# Revit family: Train_Rack-American_Standard-Town_Square-7455260_Series
name_source: partatom
category: Specialty Equipment
units: mm (PartAtom-declared; Revit-internal decimal feet)

## family parameters
Cut with Voids When Loaded = No
Host = Face
OmniClass Number = 23.40.20.21.27
OmniClass Title = Towel Bars
Part Type = Normal
Room Calculation Point = No
Round Connector Dimension = Use Diameter
Shared = Yes

## types (4) — shared parameters
Assembly Code = C1030200
Default Elevation = 40"
Description = Town Square® S 24-Inch Train Rack
Height = 4 15/16"
Installation Type = Wall Mounted
Length = 25 7/8"
Manufacturer = American Standard
Product Documentation Link = https://americanstandard.box.com
Product Page URL = https://www.americanstandard-us.com
URL = https://www.americanstandard-us.com
Warranty Information = Limited Lifetime Warranty
Width = 10 9/16"

## per-type parameters (varying)
| type | Finish | Material |
| 7455260.002 | Brass-American Standard-002-Polished Chrome | Brass-American Standard-002-Polished Chrome |
| 7455260.295 | Brass-American Standard-295-Satin Nickel | Brass-American Standard-295-Satin Nickel |
| 7455260.278 | Brass-American Standard-278-Legacy Bronze | Brass-American Standard-278-Legacy Bronze |
| 7455260.013 | Brass-American Standard-013-Polished Nickel | Brass-American Standard-013-Polished Nickel |

note: column(s) folded — value = type name in every type: Model

## geometry (parser evidence)
native form markers: Sweep x3
no freeform markers — native parametric forms only
